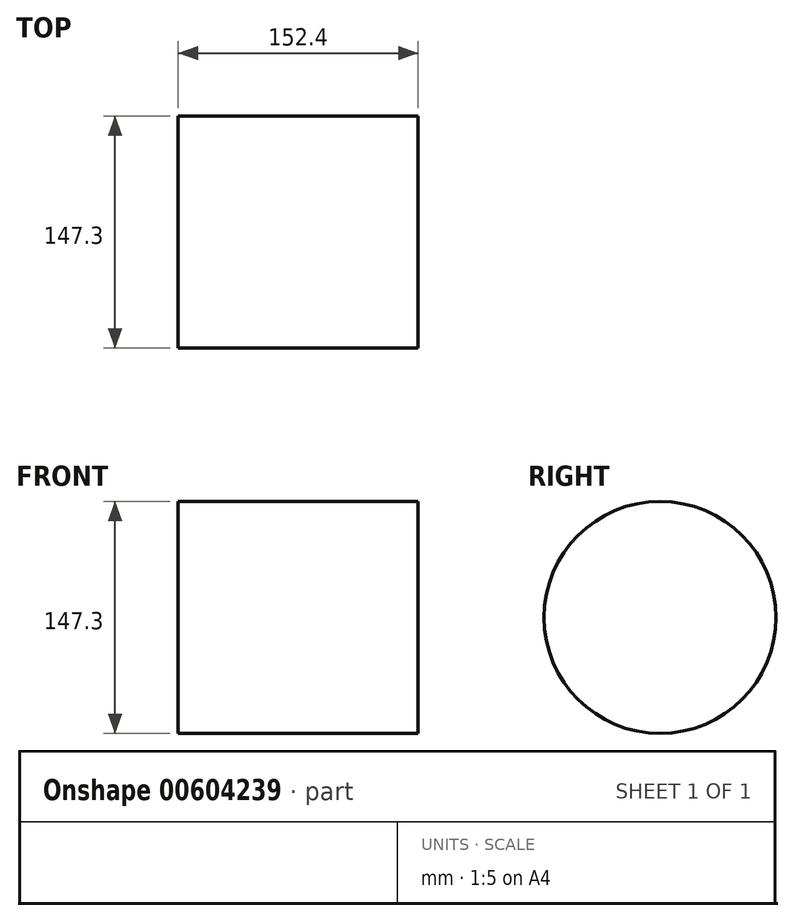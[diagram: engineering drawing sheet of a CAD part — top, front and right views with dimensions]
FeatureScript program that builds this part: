
annotation { "Feature Type Name" : "Feature", "Feature Type Description" : "" }
export const myFeature = defineFeature(function(context is Context, id is Id, definition is map)
    precondition{}
    {
        {
            var Q0;
            Q0=qCreatedBy(makeId("Right.planeOp"),FACE);
            var sketch = newSketch(context, id + "F0", { "sketchPlane" : qUnion([Q0])});
            skCircle(sketch, "E0", {"center": v(0, 0) * mm, "radius": 73.65 * mm});
            skSolve(sketch);
        }
        {
            var Q0;
            Q0=qSketchRegion(id+"F0",true);
            extrude(context, id + "F1", {"entities" : qUnion([Q0]), "depth" : 76.2 * mm, "offsetDistance" : 25.4 * mm, "hasSecondDirection" : true, "secondDirectionOppositeDirection" : true, "secondDirectionDepth" : 76.2 * mm});
        }
    });
